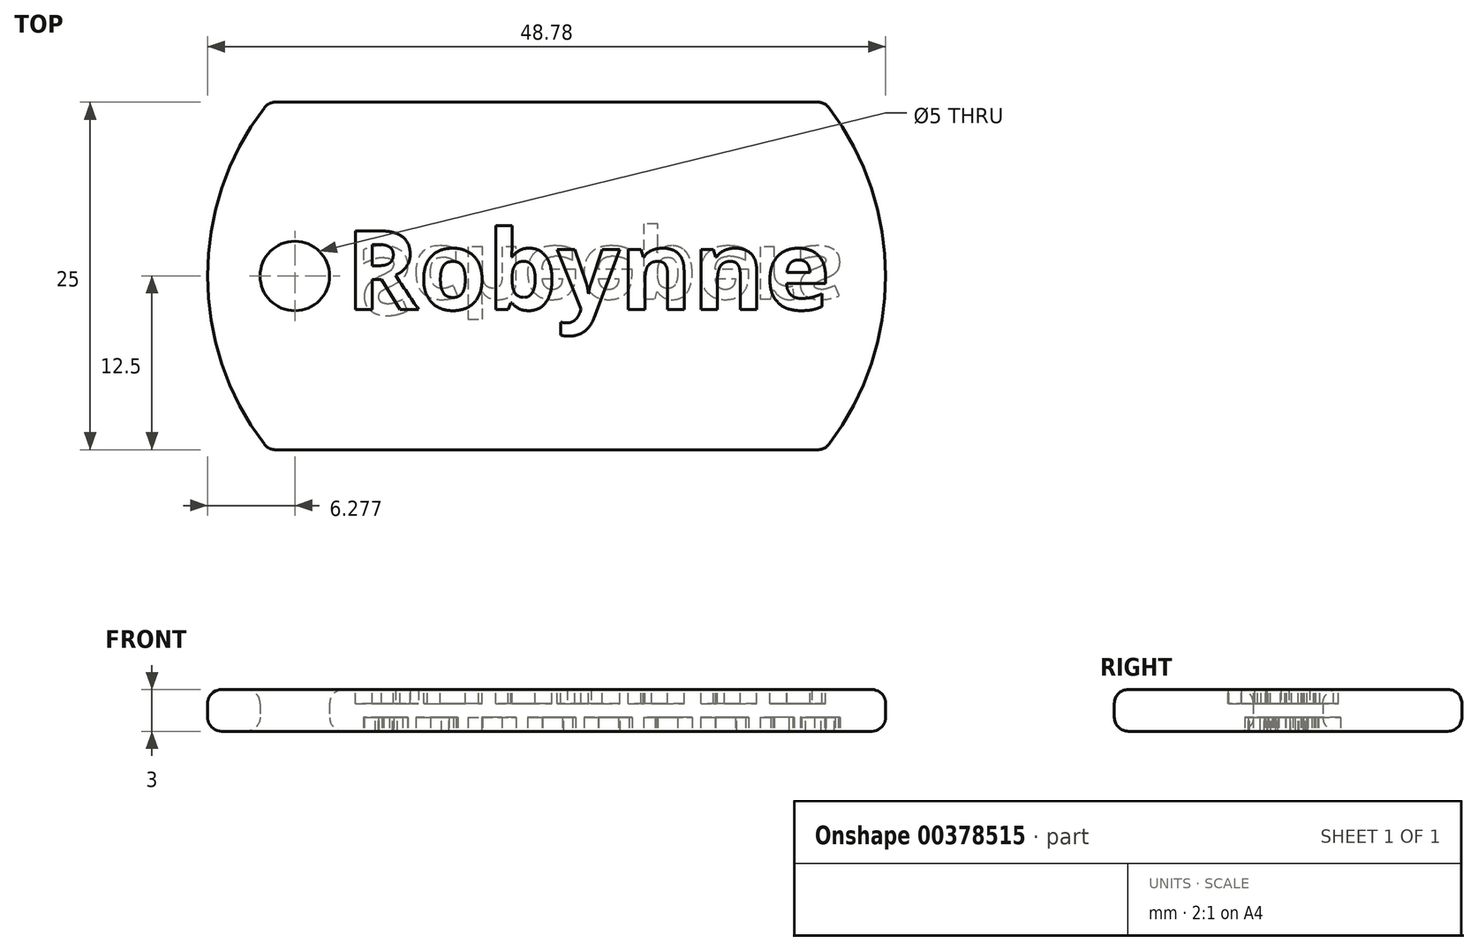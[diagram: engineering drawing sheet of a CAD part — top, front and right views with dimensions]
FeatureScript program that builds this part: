
annotation { "Feature Type Name" : "Feature", "Feature Type Description" : "" }
export const myFeature = defineFeature(function(context is Context, id is Id, definition is map)
    precondition{}
    {
        {
            var Q0;
            Q0=qCreatedBy(makeId("Top.planeOp"),FACE);
            var sketch = newSketch(context, id + "F0", { "sketchPlane" : qUnion([Q0])});
            skLineSegment(sketch, "E0.bottom", {"start": v(-20, 12.5) * mm, "end": v(20, 12.5) * mm});
            skLineSegment(sketch, "E0.top", {"start": v(-20, -12.5) * mm, "end": v(20, -12.5) * mm});
            skArc(sketch, "E1", {"start": v(-20, 12.5) * mm, "mid": v(-24.39, 0) * mm, "end": v(-20, -12.5) * mm});
            skArc(sketch, "E2", {"start": v(20, -12.5) * mm, "mid": v(24.39, 0) * mm, "end": v(20, 12.5) * mm});
            skCircle(sketch, "E3", {"center": v(-18.11, 0) * mm, "radius": 2.5 * mm});
            skSolve(sketch);
        }
        {
            var Q0;
            Q0=makeQuery(id+"F0.imprint","IMPRINT",FACE,{"disambiguationData":[TD([[makeQuery(id+"F0.imprint","IMPRINT",EDGE,{"derivedFrom":sQuery(id+"F0.wireOp",EDGE,"E0.bottom")}),-1.0]])]});
            extrude(context, id + "F1", {"entities" : qUnion([Q0]), "depth" : 3 * mm});
        }
        {
            var Q0;
            Q0=makeQuery(id+"F1.opExtrude","CAP_FACE",FACE,{"disambiguationData":[OSD([sQuery(id+"F0.wireOp",EDGE,"E0.bottom"),sQuery(id+"F0.wireOp",EDGE,"E0.top"),sQuery(id+"F0.wireOp",EDGE,"E1"),sQuery(id+"F0.wireOp",EDGE,"E2"),sQuery(id+"F0.wireOp",EDGE,"E3")])],"isStart":false});
            var sketch = newSketch(context, id + "F2", { "sketchPlane" : qUnion([Q0])});
            skText(sketch, "E4", { "text": "Robynne\n", "fontName": "OpenSans-Bold.ttf"});
            const initialGuessF2  = {"E4": [-0.01445, -0.00242, 1, 0, 0.00572]};
            skSetInitialGuess(sketch, initialGuessF2);
            skSolve(sketch);
        }
        {
            var Q0;
            Q0=qSketchRegion(id+"F2",true);
            extrude(context, id + "F3", {"entities" : qUnion([Q0]), "operationType" : NewBodyOperationType.REMOVE, "oppositeDirection" : true, "depth" : 1 * mm});
        }
        {
            var Q0;
            Q0=makeQuery(id+"F1.opExtrude","CAP_FACE",FACE,{"disambiguationData":[OSD([sQuery(id+"F0.wireOp",EDGE,"E0.bottom"),sQuery(id+"F0.wireOp",EDGE,"E0.top"),sQuery(id+"F0.wireOp",EDGE,"E1"),sQuery(id+"F0.wireOp",EDGE,"E2"),sQuery(id+"F0.wireOp",EDGE,"E3")])],"isStart":true});
            var sketch = newSketch(context, id + "F4", { "sketchPlane" : qUnion([Q0])});
            skText(sketch, "E5", { "text": "Scheepers", "fontName": "OpenSans-Bold.ttf"});
            const initialGuessF4  = {"E5": [-0.01349, -0.00211, 1, 0, 0.00494]};
            skSetInitialGuess(sketch, initialGuessF4);
            skSolve(sketch);
        }
        {
            var Q0;
            Q0=qSketchRegion(id+"F4",true);
            extrude(context, id + "F5", {"entities" : qUnion([Q0]), "operationType" : NewBodyOperationType.REMOVE, "oppositeDirection" : true, "depth" : 1 * mm});
        }
        {
            var Q0;
            Q0=makeQuery(id+"F1.opExtrude","SWEPT_FACE",FACE,{"disambiguationData":[OSD([sQuery(id+"F0.wireOp",EDGE,"E2")])]});
            var Q1;
            Q1=makeQuery(id+"F1.opExtrude","SWEPT_FACE",FACE,{"disambiguationData":[OSD([sQuery(id+"F0.wireOp",EDGE,"E0.top")])]});
            var Q2;
            Q2=makeQuery(id+"F1.opExtrude","SWEPT_FACE",FACE,{"disambiguationData":[OSD([sQuery(id+"F0.wireOp",EDGE,"E3")])]});
            var Q3;
            Q3=makeQuery(id+"F1.opExtrude","SWEPT_FACE",FACE,{"disambiguationData":[OSD([sQuery(id+"F0.wireOp",EDGE,"E1")])]});
            var Q4;
            Q4=makeQuery(id+"F1.opExtrude","SWEPT_FACE",FACE,{"disambiguationData":[OSD([sQuery(id+"F0.wireOp",EDGE,"E0.bottom")])]});
            fillet(context, id + "F6", {"entities" : qUnion([Q0, Q1, Q2, Q3, Q4]), "radius" : 1 * mm, "tangentPropagation" : true, "allowEdgeOverflow" : false});
        }
    });
